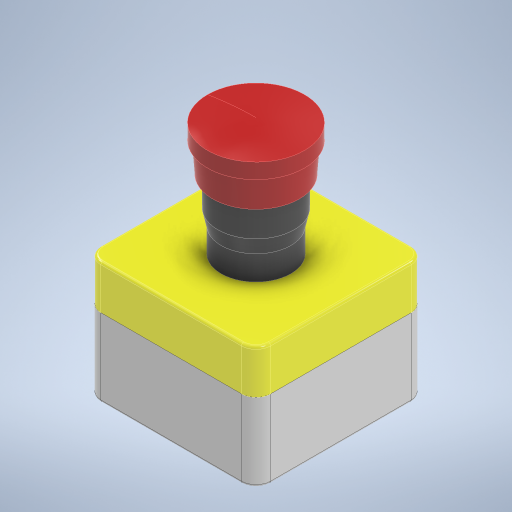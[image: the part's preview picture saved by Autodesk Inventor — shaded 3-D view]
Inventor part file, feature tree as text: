
AUTODESK INVENTOR PART (.ipt)
format: ipt  version: 2023 (Build 270158030, 158C)  size: 407,040 bytes
history: native  units: mm
features: sketch x10, extrude x9, projected_geometry x5, fillet x4, other x3, revolve x1
ambient origin geometry x8: Origin, YZ Plane, XZ Plane, XY Plane, X Axis, Y Axis, Z Axis, Center Point
bodies: Solid1 (feature_tree)
feature tree (32):
  extrude  "Extrusion1"  Depth=69.6mm
  extrude  "Extrusion2"  Depth=34.825mm
  fillet  "Fillet1"  Radius=4.6mm
  fillet  "Fillet2"  Radius=17.0mm
  fillet  "Fillet3"  Radius=6.0mm
  extrude  "Extrusion3"  Depth=17.0mm
  extrude  "Extrusion4"  Depth=1.12mm
  fillet  "Fillet4"  Radius=29.4mm
  extrude  "Extrusion5"  Depth=5.0mm
  extrude  "Extrusion6"  Depth=1.0mm TaperAngle=0.0deg
  extrude  "Extrusion7"  Depth=1.0mm
  extrude  "Extrusion8"  Depth=10.0mm TaperAngle=0.0deg
  revolve  "Revolution1"  [1 undecoded]
  extrude  "Extrusion9"  Depth=12.0mm
  sketch  "Sketch1"  dims[d0=69.65mm d1=69.6mm]
  sketch  "Sketch2"  dims[d2=34.8mm d3=34.825mm d4=4.6mm d5=17.0mm d6=6.0mm]
  projected_geometry  "Projected Loop1"
  sketch  "Sketch3"  dims[d7=6.0mm d8=17.0mm]
  projected_geometry  "Projected Loop2"
  other  "yellow"
  sketch  "Sketch4"  dims[d9=2.6mm d10=0.0mm d11=1.12mm d12=29.4mm d13=0.0mm]
  projected_geometry  "Projected Loop3"
  sketch  "Sketch5"  dims[d14=5.0mm d15=6.0mm]
  other  "black"
  sketch  "Sketch6"  dims[d16=1.0mm d17=18.0mm d18=0.0mm]
  projected_geometry  "Projected Loop4"
  sketch  "Sketch7"  dims[d19=1.1mm d20=0.0mm d21=1.0mm]
  projected_geometry  "Projected Loop5"
  sketch  "Sketch8"  dims[d22=28.6mm d23=10.0mm d24=0.0mm]
  other  "red"
  sketch  "Sketch9"  dims[d25=6.26mm d26=2.094395mm d27=12.0mm d28=0.0mm]
  sketch  "Sketch10"  dims[d29=35.5mm d30=12.0mm d31=0.698132mm d32=39.6mm d33=8.0mm d34=0.0mm d35=19.85mm d36=6.26mm d37=8.0mm d38=9.0mm d39=360.0deg]
note: 1 required parameter value undecoded (feature->parameter linkage not recoverable at this tier; creation-order binding heuristic only, values carry confidence <= 0.55)
